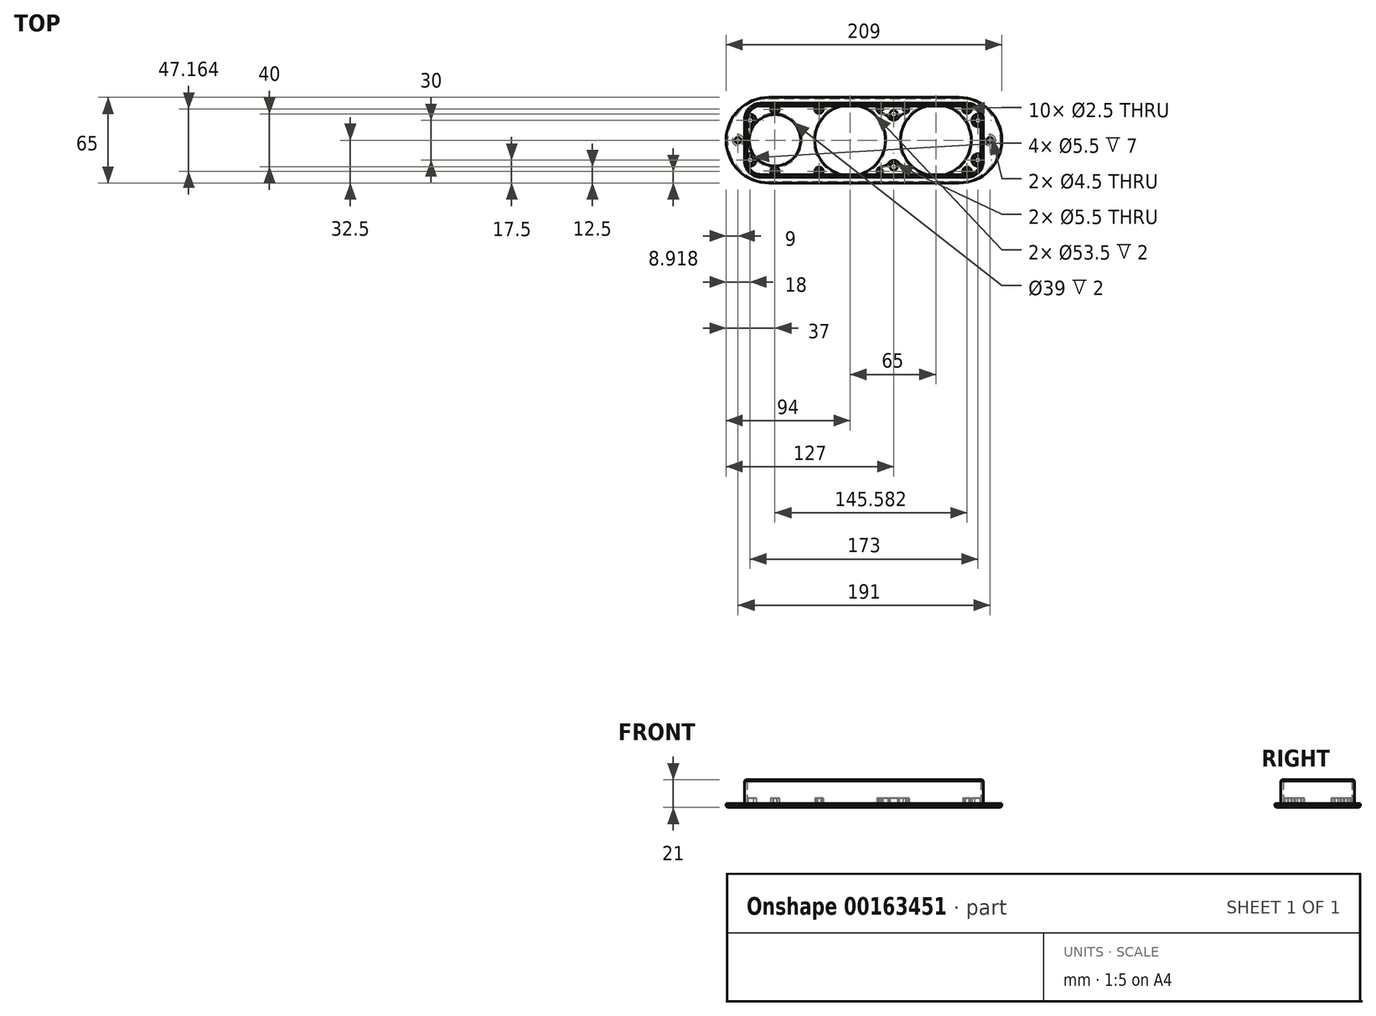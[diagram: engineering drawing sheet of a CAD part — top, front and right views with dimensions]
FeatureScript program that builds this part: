
annotation { "Feature Type Name" : "Feature", "Feature Type Description" : "" }
export const myFeature = defineFeature(function(context is Context, id is Id, definition is map)
    precondition{}
    {
        {
            var Q0;
            Q0=qCreatedBy(makeId("Top.planeOp"),FACE);
            var sketch = newSketch(context, id + "F0", { "sketchPlane" : qUnion([Q0])});
            skLineSegment(sketch, "E0.bottom", {"start": v(82.5, -29.5) * mm, "end": v(-61.5, -29.5) * mm, "construction": true});
            skLineSegment(sketch, "E0.top", {"start": v(82.5, 29.5) * mm, "end": v(-61.5, 29.5) * mm, "construction": true});
            skPoint(sketch, "E0.middle", {"position": v(0, 0) * mm});
            skCircle(sketch, "E1", {"center": v(0, 0) * mm, "radius": 26.75 * mm});
            skCircle(sketch, "E2", {"center": v(65, 0) * mm, "radius": 26.75 * mm});
            skCircle(sketch, "E3", {"center": v(-57, 0) * mm, "radius": 19.5 * mm});
            skCircle(sketch, "E4", {"center": v(-76, -15) * mm, "radius": 2.75 * mm});
            skLineSegment(sketch, "E5", {"start": v(-91, 0) * mm, "end": v(112, 0) * mm, "construction": true});
            skCircle(sketch, "E6", {"center": v(-76, 15) * mm, "radius": 2.75 * mm});
            skCircle(sketch, "E7", {"center": v(33, -20) * mm, "radius": 2.75 * mm});
            skCircle(sketch, "E8", {"center": v(33, 20) * mm, "radius": 2.75 * mm});
            skCircle(sketch, "E9", {"center": v(97, -15) * mm, "radius": 2.75 * mm});
            skCircle(sketch, "E10", {"center": v(97, 15) * mm, "radius": 2.75 * mm});
            skArc(sketch, "E11", {"start": v(-61.5, 29.5) * mm, "mid": v(-91, 0) * mm, "end": v(-61.5, -29.5) * mm, "construction": true});
            skArc(sketch, "E12", {"start": v(82.5, -29.5) * mm, "mid": v(112, 0) * mm, "end": v(82.5, 29.5) * mm, "construction": true});
            skCircle(sketch, "E13", {"center": v(-85, 0) * mm, "radius": 2.25 * mm});
            skCircle(sketch, "E14", {"center": v(106, 0) * mm, "radius": 2.25 * mm});
            skLineSegment(sketch, "E15", {"start": v(10.5, 29.5) * mm, "end": v(10.5, -29.5) * mm, "construction": true});
            skPoint(sketch, "E16", {"position": v(10.5, 0) * mm});
            skLineSegment(sketch, "E17.0", {"start": v(82.5, -32.5) * mm, "end": v(-61.5, -32.5) * mm});
            skArc(sketch, "E17.1", {"start": v(82.5, -32.5) * mm, "mid": v(115, 0) * mm, "end": v(82.5, 32.5) * mm});
            skLineSegment(sketch, "E17.2", {"start": v(82.5, 32.5) * mm, "end": v(-61.5, 32.5) * mm});
            skArc(sketch, "E17.3", {"start": v(-61.5, 32.5) * mm, "mid": v(-94, 0) * mm, "end": v(-61.5, -32.5) * mm});
            skLineSegment(sketch, "E18.0", {"start": v(82.5, 25) * mm, "end": v(-61.5, 25) * mm, "construction": true});
            skArc(sketch, "E18.1", {"start": v(82.5, -25) * mm, "mid": v(107.5, 0) * mm, "end": v(82.5, 25) * mm, "construction": true});
            skLineSegment(sketch, "E18.2", {"start": v(82.5, -25) * mm, "end": v(-61.5, -25) * mm, "construction": true});
            skArc(sketch, "E18.3", {"start": v(-61.5, 25) * mm, "mid": v(-86.5, 0) * mm, "end": v(-61.5, -25) * mm, "construction": true});
            skSolve(sketch);
        }
        {
            var Q0;
            Q0=makeQuery(id+"F0.imprint","IMPRINT",FACE,{"disambiguationData":[TD([[makeQuery(id+"F0.imprint","IMPRINT",EDGE,{"derivedFrom":sQuery(id+"F0.wireOp",EDGE,"E1")}),-1.0]])]});
            extrude(context, id + "F10", {"entities" : qUnion([Q0]), "depth" : 3 * mm});
        }
        {
            var Q0;
            Q0=makeQuery(id+"F10.opExtrude","CAP_FACE",FACE,{"disambiguationData":[OSD([sQuery(id+"F0.wireOp",EDGE,"E0.bottom"),sQuery(id+"F0.wireOp",EDGE,"E0.top"),sQuery(id+"F0.wireOp",EDGE,"E0.left"),sQuery(id+"F0.wireOp",EDGE,"E0.right"),sQuery(id+"F0.wireOp",EDGE,"E1"),sQuery(id+"F0.wireOp",EDGE,"E2"),sQuery(id+"F0.wireOp",EDGE,"E3"),sQuery(id+"F0.wireOp",EDGE,"E4"),sQuery(id+"F0.wireOp",EDGE,"E6"),sQuery(id+"F0.wireOp",EDGE,"e97acb53-c743-4d47-a917-a7d7f15044a3.1.0.0"),sQuery(id+"F0.wireOp",EDGE,"e97acb53-c743-4d47-a917-a7d7f15044a3.1.0.1"),sQuery(id+"F0.wireOp",EDGE,"e97acb53-c743-4d47-a917-a7d7f15044a3.2.0.0"),sQuery(id+"F0.wireOp",EDGE,"e97acb53-c743-4d47-a917-a7d7f15044a3.2.0.1"),sQuery(id+"F0.wireOp",EDGE,"e97acb53-c743-4d47-a917-a7d7f15044a3.3.0.0"),sQuery(id+"F0.wireOp",EDGE,"e97acb53-c743-4d47-a917-a7d7f15044a3.3.0.1")])],"isStart":false});
            var sketch = newSketch(context, id + "F1", { "sketchPlane" : qUnion([Q0])});
            skCircle(sketch, "E19.0", {"center": v(0, 0) * mm, "radius": 33.35 * mm, "construction": true});
            skCircle(sketch, "E20.0", {"center": v(65, 0) * mm, "radius": 33.35 * mm, "construction": true});
            skLineSegment(sketch, "E21", {"start": v(-94.2, 0) * mm, "end": v(115.1, 0) * mm, "construction": true});
            skLineSegment(sketch, "E22", {"start": v(41.42, -23.58) * mm, "end": v(88.58, 23.58) * mm, "construction": true});
            skLineSegment(sketch, "E23", {"start": v(41.42, 23.58) * mm, "end": v(88.58, -23.58) * mm, "construction": true});
            skPoint(sketch, "E24", {"position": v(88.58, 23.58) * mm});
            skPoint(sketch, "E25", {"position": v(88.58, -23.58) * mm});
            skPoint(sketch, "E26", {"position": v(41.42, -23.58) * mm});
            skPoint(sketch, "E27", {"position": v(41.42, 23.58) * mm});
            skLineSegment(sketch, "E28", {"start": v(-23.58, 23.58) * mm, "end": v(23.58, -23.58) * mm, "construction": true});
            skLineSegment(sketch, "E29", {"start": v(-23.58, -23.58) * mm, "end": v(23.58, 23.58) * mm, "construction": true});
            skPoint(sketch, "E30", {"position": v(23.58, 23.58) * mm});
            skPoint(sketch, "E31", {"position": v(-23.58, -23.58) * mm});
            skPoint(sketch, "E32", {"position": v(-23.58, 23.58) * mm});
            skPoint(sketch, "E33", {"position": v(23.58, -23.58) * mm});
            skLineSegment(sketch, "E34", {"start": v(-57, 32.56) * mm, "end": v(-57, -32.69) * mm, "construction": true});
            skCircle(sketch, "E35.0", {"center": v(-57, 0) * mm, "radius": 19.5 * mm, "construction": true});
            skPoint(sketch, "E36", {"position": v(-57, 23.35) * mm});
            skPoint(sketch, "E37", {"position": v(-57, -23.35) * mm});
            skSolve(sketch);
        }
        {
            var Q0;
            Q0=makeQuery(id+"F10.opExtrude","CAP_FACE",FACE,{"disambiguationData":[OSD([sQuery(id+"F0.wireOp",EDGE,"E0.bottom"),sQuery(id+"F0.wireOp",EDGE,"E0.top"),sQuery(id+"F0.wireOp",EDGE,"E1"),sQuery(id+"F0.wireOp",EDGE,"E2"),sQuery(id+"F0.wireOp",EDGE,"E3"),sQuery(id+"F0.wireOp",EDGE,"E4"),sQuery(id+"F0.wireOp",EDGE,"E6"),sQuery(id+"F0.wireOp",EDGE,"E7"),sQuery(id+"F0.wireOp",EDGE,"E8"),sQuery(id+"F0.wireOp",EDGE,"E9"),sQuery(id+"F0.wireOp",EDGE,"E10"),sQuery(id+"F0.wireOp",EDGE,"E11"),sQuery(id+"F0.wireOp",EDGE,"E12"),sQuery(id+"F0.wireOp",EDGE,"187c8602-a715-4c4d-bdd9-d6039d3960e4"),sQuery(id+"F0.wireOp",EDGE,"5191ed47-305d-4237-abde-063f77adabc3"),sQuery(id+"F0.wireOp",EDGE,"E13"),sQuery(id+"F0.wireOp",EDGE,"E14")])],"isStart":false});
            var sketch = newSketch(context, id + "F2", { "sketchPlane" : qUnion([Q0])});
            skLineSegment(sketch, "E38.bottom", {"start": v(-68, 26) * mm, "end": v(89, 26) * mm});
            skLineSegment(sketch, "E38.top", {"start": v(-68, -26) * mm, "end": v(89, -26) * mm});
            skLineSegment(sketch, "E38.left", {"start": v(-78, 16) * mm, "end": v(-78, -16) * mm});
            skLineSegment(sketch, "E38.right", {"start": v(99, 16) * mm, "end": v(99, -16) * mm});
            skLineSegment(sketch, "E39", {"start": v(-78, 0) * mm, "end": v(99, 0) * mm, "construction": true});
            skCircle(sketch, "E40.0", {"center": v(-57, 0) * mm, "radius": 19.5 * mm, "construction": true});
            skCircle(sketch, "E41.0", {"center": v(65, 0) * mm, "radius": 26.75 * mm, "construction": true});
            skPoint(sketch, "E42.visualSharp", {"position": v(-78, 26) * mm});
            skArc(sketch, "E42.filletArc", {"start": v(-68, 26) * mm, "mid": v(-75.07, 23.07) * mm, "end": v(-78, 16) * mm});
            skPoint(sketch, "E43.visualSharp", {"position": v(-78, -26) * mm});
            skArc(sketch, "E43.filletArc", {"start": v(-78, -16) * mm, "mid": v(-75.07, -23.07) * mm, "end": v(-68, -26) * mm});
            skPoint(sketch, "E44.visualSharp", {"position": v(99, -26) * mm});
            skArc(sketch, "E44.filletArc", {"start": v(89, -26) * mm, "mid": v(96.07, -23.07) * mm, "end": v(99, -16) * mm});
            skPoint(sketch, "E45.visualSharp", {"position": v(99, 26) * mm});
            skArc(sketch, "E45.filletArc", {"start": v(99, 16) * mm, "mid": v(96.07, 23.07) * mm, "end": v(89, 26) * mm});
            skArc(sketch, "E46.0", {"start": v(-68, 28) * mm, "mid": v(-76.49, 24.49) * mm, "end": v(-80, 16) * mm});
            skLineSegment(sketch, "E46.1", {"start": v(-80, 16) * mm, "end": v(-80, -16) * mm});
            skLineSegment(sketch, "E46.2", {"start": v(-68, 28) * mm, "end": v(89, 28) * mm});
            skArc(sketch, "E46.3", {"start": v(-80, -16) * mm, "mid": v(-76.49, -24.49) * mm, "end": v(-68, -28) * mm});
            skArc(sketch, "E46.4", {"start": v(101, 16) * mm, "mid": v(97.49, 24.49) * mm, "end": v(89, 28) * mm});
            skLineSegment(sketch, "E46.5", {"start": v(101, 16) * mm, "end": v(101, -16) * mm});
            skArc(sketch, "E46.6", {"start": v(89, -28) * mm, "mid": v(97.49, -24.49) * mm, "end": v(101, -16) * mm});
            skLineSegment(sketch, "E46.7", {"start": v(-68, -28) * mm, "end": v(89, -28) * mm});
            skSolve(sketch);
        }
        {
            var Q0;
            Q0 = qSketchRegion(id + "F2", true);
            extrude(context, id + "F3", {"entities" : qUnion([Q0]), "operationType" : NewBodyOperationType.ADD, "depth" : 18 * mm});
        }
        {
            var Q0;
            Q0=sQuery(id+"F1.wireOp",VERTEX,"bb7c27ac-7c7d-4624-a1fd-12c94900b50b");
            var Q1;
            Q1=sQuery(id+"F1.wireOp",VERTEX,"440de450-a3e0-481e-89b7-13e22c287d1f");
            var Q2;
            Q2=sQuery(id+"F1.wireOp",VERTEX,"19132ee3-4b6c-490e-9716-60713a6fc4e9");
            var Q3;
            Q3=sQuery(id+"F1.wireOp",VERTEX,"76f253f3-3fb2-455a-9355-407b125fa727");
            var Q4;
            Q4=sQuery(id+"F1.wireOp",VERTEX,"E32");
            var Q5;
            Q5=sQuery(id+"F1.wireOp",VERTEX,"E31");
            var Q6;
            Q6=sQuery(id+"F1.wireOp",VERTEX,"E33");
            var Q7;
            Q7=sQuery(id+"F1.wireOp",VERTEX,"E30");
            var Q8;
            Q8=sQuery(id+"F1.wireOp",VERTEX,"E27");
            var Q9;
            Q9=sQuery(id+"F1.wireOp",VERTEX,"E26");
            var Q10;
            Q10=sQuery(id+"F1.wireOp",VERTEX,"E25");
            var Q11;
            Q11=sQuery(id+"F1.wireOp",VERTEX,"E24");
            var Q12;
            Q12=sQuery(id+"F1.wireOp",VERTEX,"E36");
            var Q13;
            Q13=sQuery(id+"F1.wireOp",VERTEX,"E37");
            var Q14;
            Q14=makeQuery(id+"F10.opExtrude","SWEPT_BODY",BODY,{"disambiguationData":[OSD([sQuery(id+"F0.wireOp",EDGE,"E0.bottom"),sQuery(id+"F0.wireOp",EDGE,"E0.top"),sQuery(id+"F0.wireOp",EDGE,"E0.left"),sQuery(id+"F0.wireOp",EDGE,"E0.right"),sQuery(id+"F0.wireOp",EDGE,"E1"),sQuery(id+"F0.wireOp",EDGE,"E2"),sQuery(id+"F0.wireOp",EDGE,"E3"),sQuery(id+"F0.wireOp",EDGE,"E4"),sQuery(id+"F0.wireOp",EDGE,"E6"),sQuery(id+"F0.wireOp",EDGE,"e97acb53-c743-4d47-a917-a7d7f15044a3.1.0.0"),sQuery(id+"F0.wireOp",EDGE,"e97acb53-c743-4d47-a917-a7d7f15044a3.1.0.1"),sQuery(id+"F0.wireOp",EDGE,"e97acb53-c743-4d47-a917-a7d7f15044a3.2.0.0"),sQuery(id+"F0.wireOp",EDGE,"e97acb53-c743-4d47-a917-a7d7f15044a3.2.0.1"),sQuery(id+"F0.wireOp",EDGE,"e97acb53-c743-4d47-a917-a7d7f15044a3.3.0.0"),sQuery(id+"F0.wireOp",EDGE,"e97acb53-c743-4d47-a917-a7d7f15044a3.3.0.1")])]});
            hole(context, id + "F4", {"style" : HoleStyle.SIMPLE, "endStyle" : HoleEndStyle.BLIND, "holeDiameter" : 2.5 * mm, "holeDepth" : 25 * mm, "locations" : qUnion([Q0, Q1, Q2, Q3, Q4, Q5, Q6, Q7, Q8, Q9, Q10, Q11, Q12, Q13]), "scope" : qUnion([Q14]), "startStyle" : HoleStartStyle.SKETCH});
        }
        {
            var Q0;
            Q0=makeQuery(id+"F10.opExtrude","CAP_FACE",FACE,{"disambiguationData":[OSD([sQuery(id+"F0.wireOp",EDGE,"E1"),sQuery(id+"F0.wireOp",EDGE,"E2"),sQuery(id+"F0.wireOp",EDGE,"E3"),sQuery(id+"F0.wireOp",EDGE,"E4"),sQuery(id+"F0.wireOp",EDGE,"E6"),sQuery(id+"F0.wireOp",EDGE,"E7"),sQuery(id+"F0.wireOp",EDGE,"E8"),sQuery(id+"F0.wireOp",EDGE,"E9"),sQuery(id+"F0.wireOp",EDGE,"E10"),sQuery(id+"F0.wireOp",EDGE,"E13"),sQuery(id+"F0.wireOp",EDGE,"E14"),sQuery(id+"F0.wireOp",EDGE,"E17.0"),sQuery(id+"F0.wireOp",EDGE,"E17.1"),sQuery(id+"F0.wireOp",EDGE,"E17.2"),sQuery(id+"F0.wireOp",EDGE,"E17.3")])],"isStart":false});
            var sketch = newSketch(context, id + "F5", { "sketchPlane" : qUnion([Q0])});
            skLineSegment(sketch, "E47.0", {"start": v(-58.88, -26) * mm, "end": v(-55.12, -26) * mm});
            skArc(sketch, "E47.1", {"start": v(-77.96, -16.93) * mm, "mid": v(-77.74, -18.26) * mm, "end": v(-77.35, -19.56) * mm});
            skLineSegment(sketch, "E47.2", {"start": v(-78, 13.11) * mm, "end": v(-78, 10.7) * mm});
            skArc(sketch, "E47.3", {"start": v(-77.35, 19.56) * mm, "mid": v(-77.74, 18.26) * mm, "end": v(-77.96, 16.93) * mm});
            skLineSegment(sketch, "E47.4", {"start": v(-58.88, 26) * mm, "end": v(-55.12, 26) * mm});
            skArc(sketch, "E47.5", {"start": v(98.96, 16.93) * mm, "mid": v(98.74, 18.26) * mm, "end": v(98.35, 19.56) * mm});
            skLineSegment(sketch, "E47.6", {"start": v(99, 13.11) * mm, "end": v(99, 10.7) * mm});
            skArc(sketch, "E47.7", {"start": v(89, -26) * mm, "mid": v(89.98, -25.95) * mm, "end": v(90.95, -25.8) * mm});
            skArc(sketch, "E48.0", {"start": v(99, -13.11) * mm, "mid": v(94.25, -14.97) * mm, "end": v(98.96, -16.93) * mm});
            skArc(sketch, "E48.1", {"start": v(98.96, 16.93) * mm, "mid": v(94.25, 14.97) * mm, "end": v(99, 13.11) * mm});
            skCircle(sketch, "E48.2", {"center": v(88.58, 23.58) * mm, "radius": 1.25 * mm});
            skCircle(sketch, "E48.3", {"center": v(88.58, -23.58) * mm, "radius": 1.25 * mm});
            skCircle(sketch, "E48.4", {"center": v(41.42, -23.58) * mm, "radius": 1.25 * mm});
            skCircle(sketch, "E48.5", {"center": v(33, -20) * mm, "radius": 2.75 * mm});
            skCircle(sketch, "E48.6", {"center": v(33, 20) * mm, "radius": 2.75 * mm});
            skCircle(sketch, "E48.7", {"center": v(41.42, 23.58) * mm, "radius": 1.25 * mm});
            skCircle(sketch, "E48.8", {"center": v(23.58, 23.58) * mm, "radius": 1.25 * mm});
            skCircle(sketch, "E49.0", {"center": v(-23.58, 23.58) * mm, "radius": 1.25 * mm});
            skCircle(sketch, "E49.1", {"center": v(-23.58, -23.58) * mm, "radius": 1.25 * mm});
            skCircle(sketch, "E49.2", {"center": v(-57, -23.35) * mm, "radius": 1.25 * mm});
            skCircle(sketch, "E49.3", {"center": v(-57, 23.35) * mm, "radius": 1.25 * mm});
            skArc(sketch, "E49.4", {"start": v(-78, 13.11) * mm, "mid": v(-73.25, 14.97) * mm, "end": v(-77.96, 16.93) * mm});
            skArc(sketch, "E49.5", {"start": v(-77.96, -16.93) * mm, "mid": v(-73.25, -14.97) * mm, "end": v(-78, -13.11) * mm});
            skCircle(sketch, "E50.0", {"center": v(23.58, -23.58) * mm, "radius": 1.25 * mm});
            skArc(sketch, "E51.0", {"start": v(-25.75, 26) * mm, "mid": v(-23.58, 20.33) * mm, "end": v(-21.41, 26) * mm});
            skArc(sketch, "E52.0", {"start": v(21.41, 26) * mm, "mid": v(20.6, 22.3) * mm, "end": v(23.84, 20.34) * mm});
            skArc(sketch, "E53.0", {"start": v(41.77, 20.35) * mm, "mid": v(44.51, 22.58) * mm, "end": v(43.59, 26) * mm});
            skArc(sketch, "E54.0", {"start": v(86.41, 26) * mm, "mid": v(88.44, 20.33) * mm, "end": v(90.95, 25.8) * mm});
            skArc(sketch, "E55.0", {"start": v(90.95, -25.8) * mm, "mid": v(88.44, -20.33) * mm, "end": v(86.41, -26) * mm});
            skArc(sketch, "E56.0", {"start": v(43.59, -26) * mm, "mid": v(44.56, -22.74) * mm, "end": v(42.1, -20.4) * mm});
            skArc(sketch, "E57.0", {"start": v(23.6, -20.33) * mm, "mid": v(20.55, -22.4) * mm, "end": v(21.41, -26) * mm});
            skArc(sketch, "E58.0", {"start": v(-21.41, -26) * mm, "mid": v(-23.58, -20.33) * mm, "end": v(-25.75, -26) * mm});
            skArc(sketch, "E59.0", {"start": v(-58.88, 26) * mm, "mid": v(-57, 20.1) * mm, "end": v(-55.12, 26) * mm});
            skArc(sketch, "E60.0", {"start": v(-55.12, -26) * mm, "mid": v(-57, -20.1) * mm, "end": v(-58.88, -26) * mm});
            skArc(sketch, "E61.0", {"start": v(-77.35, -19.56) * mm, "mid": v(-71.26, -14.65) * mm, "end": v(-78, -10.7) * mm});
            skArc(sketch, "E62.0", {"start": v(-78, 10.7) * mm, "mid": v(-71.26, 14.65) * mm, "end": v(-77.35, 19.56) * mm});
            skArc(sketch, "E63.0", {"start": v(29.1, 17.3) * mm, "mid": v(33.06, 15.25) * mm, "end": v(36.97, 17.4) * mm});
            skArc(sketch, "E64.0", {"start": v(37, -17.45) * mm, "mid": v(32.6, -15.27) * mm, "end": v(28.62, -18.16) * mm});
            skArc(sketch, "E65.0", {"start": v(98.35, 19.56) * mm, "mid": v(92.26, 14.65) * mm, "end": v(99, 10.7) * mm});
            skArc(sketch, "E66.0", {"start": v(99, -10.7) * mm, "mid": v(92.26, -14.65) * mm, "end": v(98.35, -19.56) * mm});
            skArc(sketch, "E67", {"start": v(29.15, 17.22) * mm, "mid": v(26.48, 19.56) * mm, "end": v(23.03, 20.38) * mm});
            skArc(sketch, "E68", {"start": v(42.06, 20.4) * mm, "mid": v(39.21, 19.4) * mm, "end": v(36.97, 17.4) * mm});
            skArc(sketch, "E69", {"start": v(23.6, -20.33) * mm, "mid": v(26.2, -19.47) * mm, "end": v(28.62, -18.16) * mm});
            skArc(sketch, "E70", {"start": v(37, -17.45) * mm, "mid": v(39.4, -19.33) * mm, "end": v(42.24, -20.44) * mm});
            skLineSegment(sketch, "E71.trimOffspring", {"start": v(-25.75, -26) * mm, "end": v(-21.41, -26) * mm});
            skPoint(sketch, "E72.orphan", {"position": v(-68, -26) * mm});
            skLineSegment(sketch, "E73.trimOffspring", {"start": v(-78, -10.7) * mm, "end": v(-78, -13.11) * mm});
            skPoint(sketch, "E74.orphan", {"position": v(-68, 26) * mm});
            skLineSegment(sketch, "E75.trimOffspring", {"start": v(-25.75, 26) * mm, "end": v(-21.41, 26) * mm});
            skLineSegment(sketch, "E76.trimOffspring", {"start": v(21.41, 26) * mm, "end": v(43.59, 26) * mm});
            skLineSegment(sketch, "E77.trimOffspring", {"start": v(86.41, 26) * mm, "end": v(89, 26) * mm});
            skArc(sketch, "E78.trimOffspring", {"start": v(90.95, 25.8) * mm, "mid": v(89.98, 25.95) * mm, "end": v(89, 26) * mm});
            skLineSegment(sketch, "E79.trimOffspring", {"start": v(99, -10.7) * mm, "end": v(99, -13.11) * mm});
            skArc(sketch, "E80.trimOffspring", {"start": v(98.35, -19.56) * mm, "mid": v(98.74, -18.26) * mm, "end": v(98.96, -16.93) * mm});
            skLineSegment(sketch, "E81.trimOffspring", {"start": v(86.41, -26) * mm, "end": v(89, -26) * mm});
            skLineSegment(sketch, "E82.trimOffspring", {"start": v(21.41, -26) * mm, "end": v(43.59, -26) * mm});
            skPoint(sketch, "E83.orphan", {"position": v(-78, -16) * mm});
            skPoint(sketch, "E84.orphan", {"position": v(-78, 16) * mm});
            skPoint(sketch, "E85.orphan", {"position": v(99, 16) * mm});
            skPoint(sketch, "E86.orphan", {"position": v(99, -16) * mm});
            skSolve(sketch);
        }
        {
            var Q0;
            Q0 = qSketchRegion(id + "F5", true);
            extrude(context, id + "F6", {"entities" : qUnion([Q0]), "operationType" : NewBodyOperationType.ADD, "depth" : 4 * mm});
        }
        {
            var Q0;
            Q0=makeQuery(id+"F10.opExtrude","CAP_EDGE",EDGE,{"disambiguationData":[OSD([sQuery(id+"F0.wireOp",EDGE,"E13")])],"isStart":true});
            var Q1;
            Q1=makeQuery(id+"F10.opExtrude","CAP_EDGE",EDGE,{"disambiguationData":[OSD([sQuery(id+"F0.wireOp",EDGE,"E14")])],"isStart":true});
            chamfer(context, id + "F7", {"entities" : qUnion([Q0, Q1]), "width" : 2 * mm, "tangentPropagation" : true});
        }
        {
            var Q0;
            Q0=makeQuery(id+"F10.opExtrude","CAP_EDGE",EDGE,{"disambiguationData":[OSD([sQuery(id+"F0.wireOp",EDGE,"E3")])],"isStart":true});
            var Q1;
            Q1=makeQuery(id+"F10.opExtrude","CAP_EDGE",EDGE,{"disambiguationData":[OSD([sQuery(id+"F0.wireOp",EDGE,"E1")])],"isStart":true});
            var Q2;
            Q2=makeQuery(id+"F10.opExtrude","CAP_EDGE",EDGE,{"disambiguationData":[OSD([sQuery(id+"F0.wireOp",EDGE,"E2")])],"isStart":true});
            var Q3;
            Q3=makeQuery(id+"F3.opExtrude","CAP_EDGE",EDGE,{"disambiguationData":[OSD([sQuery(id+"F2.wireOp",EDGE,"E46.1")])],"isStart":false});
            chamfer(context, id + "F8", {"entities" : qUnion([Q0, Q1, Q2, Q3]), "width" : 1 * mm, "tangentPropagation" : true});
        }
        {
            var Q0;
            Q0=makeQuery(id+"F10.opExtrude","CAP_EDGE",EDGE,{"disambiguationData":[OSD([sQuery(id+"F0.wireOp",EDGE,"E17.0")])],"isStart":true});
            chamfer(context, id + "F9", {"entities" : qUnion([Q0]), "width" : 1 * mm, "tangentPropagation" : true});
        }
    });
